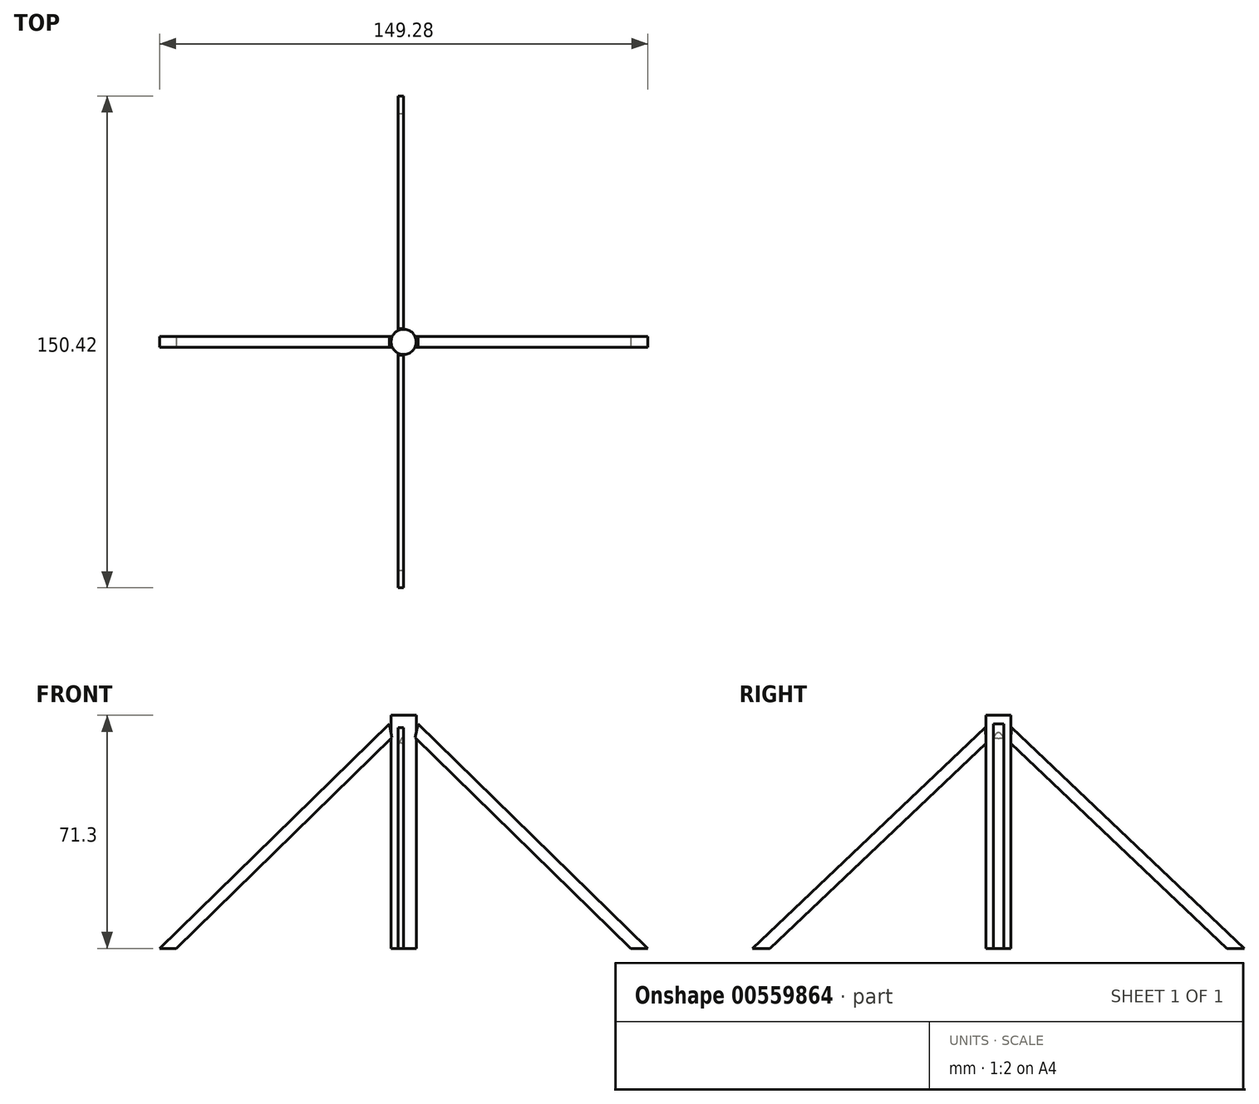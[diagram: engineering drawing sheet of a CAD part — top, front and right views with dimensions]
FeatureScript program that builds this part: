
annotation { "Feature Type Name" : "Feature", "Feature Type Description" : "" }
export const myFeature = defineFeature(function(context is Context, id is Id, definition is map)
    precondition{}
    {
        {
            var Q0;
            Q0=qCreatedBy(makeId("Top.planeOp"),FACE);
            var sketch = newSketch(context, id + "F0", { "sketchPlane" : qUnion([Q0])});
            skCircle(sketch, "E0", {"center": v(0, 0) * mm, "radius": 3.85 * mm});
            skSolve(sketch);
        }
        {
            var Q0;
            Q0=makeQuery(id+"F0.imprint","IMPRINT",FACE,{"disambiguationData":[TD([[makeQuery(id+"F0.imprint","IMPRINT",EDGE,{"derivedFrom":sQuery(id+"F0.wireOp",EDGE,"E0")}),1.0]])]});
            extrude(context, id + "F1", {"entities" : qUnion([Q0]), "depth" : 71.3 * mm, "offsetDistance" : 25 * mm});
        }
        {
            var Q0;
            Q0=qCreatedBy(makeId("Front.planeOp"),FACE);
            var sketch = newSketch(context, id + "F2", { "sketchPlane" : qUnion([Q0])});
            skLineSegment(sketch, "E1", {"start": v(-4.4, 68.7) * mm, "end": v(-74.64, 0) * mm});
            skLineSegment(sketch, "E2", {"start": v(-3.54, 64.44) * mm, "end": v(-69.45, 0) * mm});
            skLineSegment(sketch, "E3", {"start": v(-69.45, 0) * mm, "end": v(-74.64, 0) * mm});
            skLineSegment(sketch, "E4", {"start": v(-3.54, 64.44) * mm, "end": v(-4.4, 68.7) * mm});
            skSolve(sketch);
        }
        {
            var Q0;
            Q0=makeQuery(id+"F2.imprint","IMPRINT",FACE,{"disambiguationData":[TD([[makeQuery(id+"F2.imprint","IMPRINT",EDGE,{"derivedFrom":sQuery(id+"F2.wireOp",EDGE,"E1")}),1.0]])]});
            extrude(context, id + "F3", {"entities" : qUnion([Q0]), "operationType" : NewBodyOperationType.ADD, "oppositeDirection" : true, "depth" : 1.6 * mm, "offsetDistance" : 25 * mm});
        }
        {
            var Q0;
            Q0=makeQuery(id+"F1.opExtrude","SWEPT_BODY",BODY,{"disambiguationData":[OSD([sQuery(id+"F0.wireOp",EDGE,"E0")])]});
            var Q1;
            Q1=qCreatedBy(makeId("Right.planeOp"),FACE);
            mirror(context, id + "F4", {"operationType" : NewBodyOperationType.ADD, "entities" : qUnion([Q0]), "mirrorPlane" : qUnion([Q1])});
        }
        {
            var Q0;
            Q0=qCreatedBy(makeId("Right.planeOp"),FACE);
            var sketch = newSketch(context, id + "F5", { "sketchPlane" : qUnion([Q0])});
            skPoint(sketch, "E5.start.orphan", {"position": v(-60.76, 0) * mm});
            skLineSegment(sketch, "E6", {"start": v(-4.1, 67.56) * mm, "end": v(-75.2, 0) * mm});
            skLineSegment(sketch, "E7", {"start": v(-75.2, 0) * mm, "end": v(-69.83, 0) * mm});
            skLineSegment(sketch, "E8", {"start": v(-69.83, 0) * mm, "end": v(-3.68, 62.86) * mm});
            skLineSegment(sketch, "E9", {"start": v(-3.68, 62.86) * mm, "end": v(-4.1, 67.56) * mm});
            skSolve(sketch);
        }
        {
            var Q0;
            Q0=makeQuery(id+"F5.imprint","IMPRINT",FACE,{"disambiguationData":[TD([[makeQuery(id+"F5.imprint","IMPRINT",EDGE,{"derivedFrom":sQuery(id+"F5.wireOp",EDGE,"E6")}),1.0]])]});
            extrude(context, id + "F6", {"entities" : qUnion([Q0]), "operationType" : NewBodyOperationType.ADD, "oppositeDirection" : true, "depth" : 1.7 * mm, "offsetDistance" : 25 * mm});
        }
        {
            var Q0;
            Q0=makeQuery(id+"F1.opExtrude","SWEPT_BODY",BODY,{"disambiguationData":[OSD([sQuery(id+"F0.wireOp",EDGE,"E0")])]});
            var Q1;
            Q1=qCreatedBy(makeId("Front.planeOp"),FACE);
            mirror(context, id + "F7", {"operationType" : NewBodyOperationType.ADD, "entities" : qUnion([Q0]), "mirrorPlane" : qUnion([Q1])});
        }
    });
